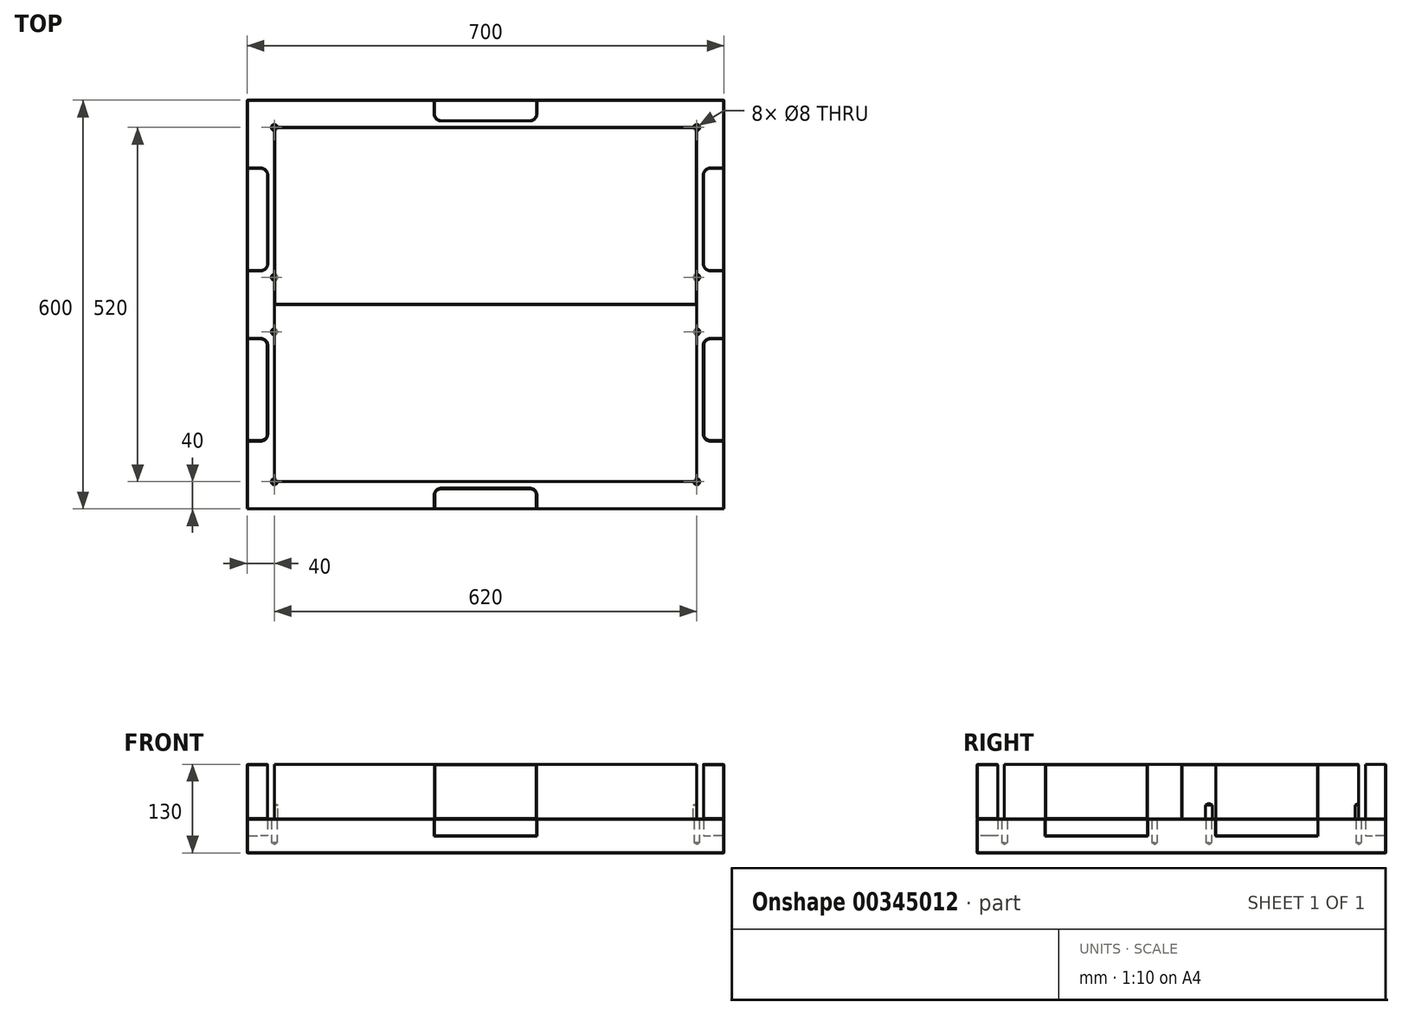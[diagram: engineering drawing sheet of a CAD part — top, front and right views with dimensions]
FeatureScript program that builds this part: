
annotation { "Feature Type Name" : "Feature", "Feature Type Description" : "" }
export const myFeature = defineFeature(function(context is Context, id is Id, definition is map)
    precondition{}
    {
        {
            var Q0;
            Q0=qCreatedBy(makeId("Top.planeOp"),FACE);
            var sketch = newSketch(context, id + "F0", { "sketchPlane" : qUnion([Q0])});
            skLineSegment(sketch, "E0", {"start": v(-350, 0) * mm, "end": v(350, 0) * mm, "construction": true});
            skLineSegment(sketch, "E1.bottom", {"start": v(350, -50) * mm, "end": v(330, -50) * mm});
            skLineSegment(sketch, "E1.top", {"start": v(350, -200) * mm, "end": v(330, -200) * mm});
            skLineSegment(sketch, "E1.left", {"start": v(350, -50) * mm, "end": v(350, -200) * mm});
            skLineSegment(sketch, "E1.right", {"start": v(320, -60) * mm, "end": v(320, -190) * mm});
            skPoint(sketch, "E2.visualSharp", {"position": v(320, -200) * mm});
            skArc(sketch, "E2.filletArc", {"start": v(320, -190) * mm, "mid": v(322.93, -197.07) * mm, "end": v(330, -200) * mm});
            skPoint(sketch, "E3.visualSharp", {"position": v(320, -50) * mm});
            skArc(sketch, "E3.filletArc", {"start": v(330, -50) * mm, "mid": v(322.93, -52.93) * mm, "end": v(320, -60) * mm});
            skLineSegment(sketch, "E4", {"start": v(0, 300) * mm, "end": v(0, -300) * mm, "construction": true});
            skLineSegment(sketch, "E5.MirrorCS", {"start": v(-350, -50) * mm, "end": v(-330, -50) * mm});
            skLineSegment(sketch, "E6.MirrorCS", {"start": v(-320, -60) * mm, "end": v(-320, -190) * mm});
            skArc(sketch, "E7.MirrorCS", {"start": v(-320, -190) * mm, "mid": v(-322.93, -197.07) * mm, "end": v(-330, -200) * mm});
            skArc(sketch, "E8.MirrorCS", {"start": v(-330, -50) * mm, "mid": v(-322.93, -52.93) * mm, "end": v(-320, -60) * mm});
            skLineSegment(sketch, "E9.MirrorCS", {"start": v(-350, -200) * mm, "end": v(-330, -200) * mm});
            skPoint(sketch, "E10", {"position": v(-310, 260) * mm});
            skPoint(sketch, "E11", {"position": v(310, 260) * mm});
            skPoint(sketch, "E12", {"position": v(310, -260) * mm});
            skPoint(sketch, "E13", {"position": v(-310, -260) * mm});
            skLineSegment(sketch, "E14.bottom", {"start": v(350, 300) * mm, "end": v(-350, 300) * mm});
            skLineSegment(sketch, "E14.top", {"start": v(350, -300) * mm, "end": v(-350, -300) * mm});
            skLineSegment(sketch, "E14.left", {"start": v(350, 300) * mm, "end": v(350, -300) * mm});
            skLineSegment(sketch, "E14.right", {"start": v(-350, 300) * mm, "end": v(-350, -300) * mm});
            skPoint(sketch, "E14.middle", {"position": v(0, 0) * mm});
            skLineSegment(sketch, "E15", {"start": v(-350, 125) * mm, "end": v(350, 125) * mm, "construction": true});
            skLineSegment(sketch, "E16", {"start": v(-350, -125) * mm, "end": v(350, -125) * mm, "construction": true});
            skLineSegment(sketch, "E17", {"start": v(320, -125) * mm, "end": v(350, -125) * mm, "construction": true});
            skLineSegment(sketch, "E18.bottom", {"start": v(330, 200) * mm, "end": v(350, 200) * mm});
            skLineSegment(sketch, "E18.top", {"start": v(330, 50) * mm, "end": v(350, 50) * mm});
            skLineSegment(sketch, "E18.left", {"start": v(320, 190) * mm, "end": v(320, 60) * mm});
            skLineSegment(sketch, "E18.right", {"start": v(350, 200) * mm, "end": v(350, 50) * mm});
            skLineSegment(sketch, "E19", {"start": v(320, 125) * mm, "end": v(350, 125) * mm, "construction": true});
            skPoint(sketch, "E20.visualSharp", {"position": v(320, 200) * mm});
            skArc(sketch, "E20.filletArc", {"start": v(330, 200) * mm, "mid": v(322.93, 197.07) * mm, "end": v(320, 190) * mm});
            skPoint(sketch, "E21.visualSharp", {"position": v(320, 50) * mm});
            skArc(sketch, "E21.filletArc", {"start": v(320, 60) * mm, "mid": v(322.93, 52.93) * mm, "end": v(330, 50) * mm});
            skLineSegment(sketch, "E22.bottom", {"start": v(-350, 200) * mm, "end": v(-330, 200) * mm});
            skLineSegment(sketch, "E22.top", {"start": v(-350, 50) * mm, "end": v(-330, 50) * mm});
            skLineSegment(sketch, "E22.left", {"start": v(-350, 200) * mm, "end": v(-350, 50) * mm});
            skLineSegment(sketch, "E22.right", {"start": v(-320, 190) * mm, "end": v(-320, 60) * mm});
            skLineSegment(sketch, "E23", {"start": v(-350, 125) * mm, "end": v(-320, 125) * mm, "construction": true});
            skPoint(sketch, "E24.visualSharp", {"position": v(-320, 200) * mm});
            skArc(sketch, "E24.filletArc", {"start": v(-320, 190) * mm, "mid": v(-322.93, 197.07) * mm, "end": v(-330, 200) * mm});
            skPoint(sketch, "E25.visualSharp", {"position": v(-320, 50) * mm});
            skArc(sketch, "E25.filletArc", {"start": v(-330, 50) * mm, "mid": v(-322.93, 52.93) * mm, "end": v(-320, 60) * mm});
            skLineSegment(sketch, "E26.bottom", {"start": v(-75, 300) * mm, "end": v(75, 300) * mm});
            skLineSegment(sketch, "E26.top", {"start": v(-65, 270) * mm, "end": v(65, 270) * mm});
            skLineSegment(sketch, "E26.left", {"start": v(-75, 300) * mm, "end": v(-75, 280) * mm});
            skLineSegment(sketch, "E26.right", {"start": v(75, 300) * mm, "end": v(75, 280) * mm});
            skLineSegment(sketch, "E27", {"start": v(0, 300) * mm, "end": v(0, 270) * mm, "construction": true});
            skPoint(sketch, "E28.visualSharp", {"position": v(-75, 270) * mm});
            skArc(sketch, "E28.filletArc", {"start": v(-75, 280) * mm, "mid": v(-72.07, 272.93) * mm, "end": v(-65, 270) * mm});
            skPoint(sketch, "E29.visualSharp", {"position": v(75, 270) * mm});
            skArc(sketch, "E29.filletArc", {"start": v(65, 270) * mm, "mid": v(72.07, 272.93) * mm, "end": v(75, 280) * mm});
            skLineSegment(sketch, "E30.bottom", {"start": v(-65, -270) * mm, "end": v(65, -270) * mm});
            skLineSegment(sketch, "E30.top", {"start": v(-75, -300) * mm, "end": v(75, -300) * mm});
            skLineSegment(sketch, "E30.left", {"start": v(-75, -280) * mm, "end": v(-75, -300) * mm});
            skLineSegment(sketch, "E30.right", {"start": v(75, -280) * mm, "end": v(75, -300) * mm});
            skLineSegment(sketch, "E31", {"start": v(0, -270) * mm, "end": v(0, -300) * mm, "construction": true});
            skPoint(sketch, "E32.visualSharp", {"position": v(-75, -270) * mm});
            skArc(sketch, "E32.filletArc", {"start": v(-65, -270) * mm, "mid": v(-72.07, -272.93) * mm, "end": v(-75, -280) * mm});
            skPoint(sketch, "E33.visualSharp", {"position": v(75, -270) * mm});
            skArc(sketch, "E33.filletArc", {"start": v(75, -280) * mm, "mid": v(72.07, -272.93) * mm, "end": v(65, -270) * mm});
            skSolve(sketch);
        }
        {
            var Q0;
            {var subQ14=sQuery(id+"F0.wireOp",EDGE,"E1.bottom");Q0=makeQuery(id+"F0.imprint","IMPRINT",FACE,{"disambiguationData":[TD([[makeQuery(id+"F0.imprint","IMPRINT",EDGE,{"derivedFrom":subQ14}),-1.0]])]});}
            extrude(context, id + "F1", {"entities" : qUnion([Q0]), "offsetDistance" : 25 * mm, "depth" : 50 * mm});
        }
        {
            var Q0;
            Q0=makeQuery(id+"F1.opExtrude","CAP_FACE",FACE,{"disambiguationData":[OSD([sQuery(id+"F0.wireOp",EDGE,"E1.bottom"),sQuery(id+"F0.wireOp",EDGE,"E1.top"),sQuery(id+"F0.wireOp",EDGE,"E1.right"),sQuery(id+"F0.wireOp",EDGE,"E2.filletArc"),sQuery(id+"F0.wireOp",EDGE,"E3.filletArc"),sQuery(id+"F0.wireOp",EDGE,"E5.MirrorCS"),sQuery(id+"F0.wireOp",EDGE,"E6.MirrorCS"),sQuery(id+"F0.wireOp",EDGE,"E7.MirrorCS"),sQuery(id+"F0.wireOp",EDGE,"E8.MirrorCS"),sQuery(id+"F0.wireOp",EDGE,"E9.MirrorCS"),sQuery(id+"F0.wireOp",EDGE,"E14.bottom"),sQuery(id+"F0.wireOp",EDGE,"E14.top"),sQuery(id+"F0.wireOp",EDGE,"E14.left"),sQuery(id+"F0.wireOp",EDGE,"E14.right")])],"isStart":false});
            var sketch = newSketch(context, id + "F2", { "sketchPlane" : qUnion([Q0])});
            skLineSegment(sketch, "E34.bottom", {"start": v(-350, 300) * mm, "end": v(350, 300) * mm});
            skLineSegment(sketch, "E34.top", {"start": v(-350, -300) * mm, "end": v(350, -300) * mm});
            skLineSegment(sketch, "E34.left", {"start": v(-350, 300) * mm, "end": v(-350, -300) * mm});
            skLineSegment(sketch, "E34.right", {"start": v(350, 300) * mm, "end": v(350, -300) * mm});
            skLineSegment(sketch, "E35.0", {"start": v(-310, 260) * mm, "end": v(310, 260) * mm});
            skLineSegment(sketch, "E35.1", {"start": v(-310, 260) * mm, "end": v(-310, -260) * mm});
            skLineSegment(sketch, "E35.2", {"start": v(-310, -260) * mm, "end": v(310, -260) * mm});
            skLineSegment(sketch, "E35.3", {"start": v(310, 260) * mm, "end": v(310, -260) * mm});
            skLineSegment(sketch, "E36", {"start": v(350, 0) * mm, "end": v(-350, 0) * mm});
            skLineSegment(sketch, "E37", {"start": v(310, 40) * mm, "end": v(-310, 40) * mm});
            skLineSegment(sketch, "E38", {"start": v(310, -40) * mm, "end": v(-310, -40) * mm});
            skSolve(sketch);
        }
        {
            var Q0;
            {var subQ9=sQuery(id+"F2.wireOp",EDGE,"E35.2");Q0=makeQuery(id+"F2.imprint","IMPRINT",FACE,{"disambiguationData":[TD([[makeQuery(id+"F2.imprint","IMPRINT",EDGE,{"derivedFrom":subQ9}),-1.0]])]});}
            var Q1;
            {var subQ1=makeQuery(id+"F1.opExtrude","CAP_EDGE",EDGE,{"disambiguationData":[OSD([sQuery(id+"F0.wireOp",EDGE,"E1.bottom")])],"isStart":false});Q1=makeQuery(id+"F2.imprint","IMPRINT",FACE,{"disambiguationData":[TD([[makeQuery(id+"F2.imprint","IMPRINT",EDGE,{"derivedFrom":subQ1}),1.0]])]});}
            var Q2;
            Q2=makeQuery(id+"F2.imprint","IMPRINT",FACE,{"disambiguationData":[TD([[makeQuery(id+"F2.imprint","IMPRINT",EDGE,{"derivedFrom":makeQuery(id+"F1.opExtrude","CAP_EDGE",EDGE,{"disambiguationData":[OSD([sQuery(id+"F0.wireOp",EDGE,"E30.bottom")])],"isStart":false})}),-1.0]])]});
            var Q3;
            {var subQ0=makeQuery(id+"F1.opExtrude","CAP_EDGE",EDGE,{"disambiguationData":[OSD([sQuery(id+"F0.wireOp",EDGE,"E5.MirrorCS")])],"isStart":false});Q3=makeQuery(id+"F2.imprint","IMPRINT",FACE,{"disambiguationData":[TD([[makeQuery(id+"F2.imprint","IMPRINT",EDGE,{"derivedFrom":subQ0}),-1.0]])]});}
            var Q4;
            {var subQ0=sQuery(id+"F2.wireOp",EDGE,"E35.2");Q4=makeQuery(id+"F2.imprint","IMPRINT",FACE,{"disambiguationData":[TD([[makeQuery(id+"F2.imprint","IMPRINT",EDGE,{"derivedFrom":subQ0}),1.0]])]});}
            var Q5;
            {var subQ0=sQuery(id+"F2.wireOp",EDGE,"E38");Q5=makeQuery(id+"F2.imprint","IMPRINT",FACE,{"disambiguationData":[TD([[makeQuery(id+"F2.imprint","IMPRINT",EDGE,{"derivedFrom":subQ0}),-1.0]])]});}
            extrude(context, id + "F3", {"entities" : qUnion([Q0, Q1, Q2, Q3, Q4, Q5]), "flatOperationType" : FlatOperationType.REMOVE, "offsetDistance" : 25 * mm, "depth" : 80 * mm, "domain" : OperationDomain.MODEL});
        }
        {
            var Q0;
            {var subQ8=sQuery(id+"F2.wireOp",EDGE,"E35.0");Q0=makeQuery(id+"F2.imprint","IMPRINT",FACE,{"disambiguationData":[TD([[makeQuery(id+"F2.imprint","IMPRINT",EDGE,{"derivedFrom":subQ8}),1.0]])]});}
            var Q1;
            {var subQ0=makeQuery(id+"F1.opExtrude","CAP_EDGE",EDGE,{"disambiguationData":[OSD([sQuery(id+"F0.wireOp",EDGE,"E18.bottom")])],"isStart":false});Q1=makeQuery(id+"F2.imprint","IMPRINT",FACE,{"disambiguationData":[TD([[makeQuery(id+"F2.imprint","IMPRINT",EDGE,{"derivedFrom":subQ0}),-1.0]])]});}
            var Q2;
            Q2=makeQuery(id+"F2.imprint","IMPRINT",FACE,{"disambiguationData":[TD([[makeQuery(id+"F2.imprint","IMPRINT",EDGE,{"derivedFrom":makeQuery(id+"F1.opExtrude","CAP_EDGE",EDGE,{"disambiguationData":[OSD([sQuery(id+"F0.wireOp",EDGE,"E26.top")])],"isStart":false})}),1.0]])]});
            var Q3;
            {var subQ1=makeQuery(id+"F1.opExtrude","CAP_EDGE",EDGE,{"disambiguationData":[OSD([sQuery(id+"F0.wireOp",EDGE,"E22.bottom")])],"isStart":false});Q3=makeQuery(id+"F2.imprint","IMPRINT",FACE,{"disambiguationData":[TD([[makeQuery(id+"F2.imprint","IMPRINT",EDGE,{"derivedFrom":subQ1}),-1.0]])]});}
            var Q4;
            {var subQ0=sQuery(id+"F2.wireOp",EDGE,"E35.0");Q4=makeQuery(id+"F2.imprint","IMPRINT",FACE,{"disambiguationData":[TD([[makeQuery(id+"F2.imprint","IMPRINT",EDGE,{"derivedFrom":subQ0}),-1.0]])]});}
            var Q5;
            {var subQ0=sQuery(id+"F2.wireOp",EDGE,"E37");Q5=makeQuery(id+"F2.imprint","IMPRINT",FACE,{"disambiguationData":[TD([[makeQuery(id+"F2.imprint","IMPRINT",EDGE,{"derivedFrom":subQ0}),1.0]])]});}
            extrude(context, id + "F4", {"entities" : qUnion([Q0, Q1, Q2, Q3, Q4, Q5]), "flatOperationType" : FlatOperationType.REMOVE, "depth" : 80 * mm, "offsetDistance" : 25 * mm, "domain" : OperationDomain.MODEL});
        }
        {
            var Q0;
            Q0=makeQuery(id+"F3.opExtrude","CAP_FACE",FACE,{"disambiguationData":[OSD([sQuery(id+"F2.wireOp",EDGE,"E34.bottom"),sQuery(id+"F2.wireOp",EDGE,"E34.top"),sQuery(id+"F2.wireOp",EDGE,"E34.left"),sQuery(id+"F2.wireOp",EDGE,"E34.right")])],"isStart":false});
            var Q1;
            Q1=makeQuery(id+"F3.opExtrude","CAP_FACE",FACE,{"disambiguationData":[OSD([sQuery(id+"F2.wireOp",EDGE,"E34.bottom"),sQuery(id+"F2.wireOp",EDGE,"E34.top"),sQuery(id+"F2.wireOp",EDGE,"E34.left"),sQuery(id+"F2.wireOp",EDGE,"E34.right")])],"isStart":true});
            var Q2;
            Q2=makeQuery(id+"F3.opExtrude","SWEPT_EDGE",EDGE,{"disambiguationData":[OSD([sQuery(id+"F2.wireOp",EDGE,"E34.bottom"),sQuery(id+"F2.wireOp",EDGE,"E34.right")])]});
            var Q3;
            Q3=makeQuery(id+"F3.opExtrude","SWEPT_EDGE",EDGE,{"disambiguationData":[OSD([sQuery(id+"F2.wireOp",EDGE,"E34.bottom"),sQuery(id+"F2.wireOp",EDGE,"E34.left")])]});
            var Q4;
            Q4=makeQuery(id+"F3.opExtrude","SWEPT_EDGE",EDGE,{"disambiguationData":[OSD([sQuery(id+"F2.wireOp",EDGE,"E34.top"),sQuery(id+"F2.wireOp",EDGE,"E34.left")])]});
            var Q5;
            Q5=makeQuery(id+"F3.opExtrude","SWEPT_EDGE",EDGE,{"disambiguationData":[OSD([sQuery(id+"F2.wireOp",EDGE,"E34.top"),sQuery(id+"F2.wireOp",EDGE,"E34.right")])]});
            var Q6;
            Q6=makeQuery(id+"F4.opExtrude","CAP_EDGE",EDGE,{"disambiguationData":[OSD([sQuery(id+"F2.wireOp",EDGE,"E34.right")])],"isStart":false});
            var Q7;
            Q7=makeQuery(id+"F4.opExtrude","CAP_EDGE",EDGE,{"disambiguationData":[OSD([sQuery(id+"F2.wireOp",EDGE,"E34.bottom")])],"isStart":false});
            var Q8;
            Q8=makeQuery(id+"F4.opExtrude","CAP_EDGE",EDGE,{"disambiguationData":[OSD([sQuery(id+"F2.wireOp",EDGE,"E36")])],"isStart":false});
            var Q9;
            Q9=makeQuery(id+"F4.opExtrude","CAP_EDGE",EDGE,{"disambiguationData":[OSD([sQuery(id+"F2.wireOp",EDGE,"E34.left")])],"isStart":false});
            var Q10;
            Q10=makeQuery(id+"F4.opExtrude","SWEPT_EDGE",EDGE,{"disambiguationData":[OSD([sQuery(id+"F2.wireOp",EDGE,"E34.left"),sQuery(id+"F2.wireOp",EDGE,"E36")])]});
            var Q11;
            Q11=makeQuery(id+"F4.opExtrude","CAP_FACE",FACE,{"disambiguationData":[OSD([sQuery(id+"F2.wireOp",EDGE,"E34.bottom"),sQuery(id+"F2.wireOp",EDGE,"E34.left"),sQuery(id+"F2.wireOp",EDGE,"E34.right"),sQuery(id+"F2.wireOp",EDGE,"E36")])],"isStart":false});
            var Q12;
            Q12=makeQuery(id+"F4.opExtrude","SWEPT_EDGE",EDGE,{"disambiguationData":[OSD([sQuery(id+"F2.wireOp",EDGE,"E34.bottom"),sQuery(id+"F2.wireOp",EDGE,"E34.right")])]});
            var Q13;
            Q13=makeQuery(id+"F4.opExtrude","SWEPT_EDGE",EDGE,{"disambiguationData":[OSD([sQuery(id+"F2.wireOp",EDGE,"E34.bottom"),sQuery(id+"F2.wireOp",EDGE,"E34.left")])]});
            chamfer(context, id + "F5", {"entities" : qUnion([Q0, Q1, Q2, Q3, Q4, Q5, Q6, Q7, Q8, Q9, Q10, Q11, Q12, Q13]), "width" : 0.5 * mm, "tangentPropagation" : true});
        }
        {
            var Q0;
            Q0=sQuery(id+"F2.wireOp",VERTEX,"E35.1.start");
            var Q1;
            Q1=sQuery(id+"F2.wireOp",VERTEX,"E35.0.end");
            var Q2;
            Q2=sQuery(id+"F2.wireOp",VERTEX,"E35.3.end");
            var Q3;
            Q3=sQuery(id+"F2.wireOp",VERTEX,"E35.2.start");
            var Q4;
            Q4=sQuery(id+"F2.wireOp",VERTEX,"E37.start");
            var Q5;
            Q5=sQuery(id+"F2.wireOp",VERTEX,"E38.end");
            var Q6;
            Q6=sQuery(id+"F2.wireOp",VERTEX,"E38.start");
            var Q7;
            Q7=sQuery(id+"F2.wireOp",VERTEX,"E37.end");
            var Q8;
            Q8=makeQuery(id+"F3.opExtrude","SWEPT_BODY",BODY,{"disambiguationData":[OSD([sQuery(id+"F2.wireOp",EDGE,"E34.bottom"),sQuery(id+"F2.wireOp",EDGE,"E34.top"),sQuery(id+"F2.wireOp",EDGE,"E34.left"),sQuery(id+"F2.wireOp",EDGE,"E34.right")])]});
            var Q9;
            Q9=makeQuery(id+"F4.opExtrude","SWEPT_BODY",BODY,{"disambiguationData":[OSD([sQuery(id+"F2.wireOp",EDGE,"E34.bottom"),sQuery(id+"F2.wireOp",EDGE,"E34.left"),sQuery(id+"F2.wireOp",EDGE,"E34.right"),sQuery(id+"F2.wireOp",EDGE,"E36")])]});
            hole(context, id + "F6", {"style" : HoleStyle.SIMPLE, "endStyle" : HoleEndStyle.BLIND, "oppositeDirection" : true, "holeDiameter" : 10 * mm, "majorDiameter" : 5 * mm, "holeDepth" : 20 * mm, "isTappedThrough" : true, "tappedDepth" : 12 * mm, "tapClearance" : 3, "locations" : qUnion([Q0, Q1, Q2, Q3, Q4, Q5, Q6, Q7]), "scope" : qUnion([Q8, Q9]), "startStyle" : HoleStartStyle.PART});
        }
        {
            var Q0;
            Q0 = qSketchRegion(id + "F0", true);
            var Q1;
            Q1 = qConstructionFilter(qBodyType(qCreatedBy(id + "F0" ,EDGE), BodyType.WIRE), ConstructionObject.NO);
            extrude(context, id + "F7", {"entities" : qUnion([Q0]), "operationType" : NewBodyOperationType.ADD, "surfaceEntities" : qUnion([Q1]), "offsetDistance" : 25 * mm, "depth" : 25 * mm});
        }
        {
            var Q0;
            Q0=sQuery(id+"F2.wireOp",VERTEX,"E35.1.start");
            var Q1;
            Q1=sQuery(id+"F2.wireOp",VERTEX,"E35.0.end");
            var Q2;
            Q2=sQuery(id+"F2.wireOp",VERTEX,"E35.3.end");
            var Q3;
            Q3=sQuery(id+"F2.wireOp",VERTEX,"E35.2.start");
            var Q4;
            Q4=sQuery(id+"F2.wireOp",VERTEX,"E37.start");
            var Q5;
            Q5=sQuery(id+"F2.wireOp",VERTEX,"E37.end");
            var Q6;
            Q6=sQuery(id+"F2.wireOp",VERTEX,"E38.end");
            var Q7;
            Q7=sQuery(id+"F2.wireOp",VERTEX,"E38.start");
            var Q8;
            Q8=makeQuery(id+"F1.opExtrude","SWEPT_BODY",BODY,{"disambiguationData":[OSD([sQuery(id+"F0.wireOp",EDGE,"9696f999-dd8b-4db2-95aa-c8651f8d9f2f.bottom"),sQuery(id+"F0.wireOp",EDGE,"9696f999-dd8b-4db2-95aa-c8651f8d9f2f.top"),sQuery(id+"F0.wireOp",EDGE,"9696f999-dd8b-4db2-95aa-c8651f8d9f2f.left"),sQuery(id+"F0.wireOp",EDGE,"9696f999-dd8b-4db2-95aa-c8651f8d9f2f.right"),sQuery(id+"F0.wireOp",EDGE,"E1.bottom"),sQuery(id+"F0.wireOp",EDGE,"E1.top"),sQuery(id+"F0.wireOp",EDGE,"E1.right"),sQuery(id+"F0.wireOp",EDGE,"E2.filletArc"),sQuery(id+"F0.wireOp",EDGE,"E3.filletArc"),sQuery(id+"F0.wireOp",EDGE,"E5.MirrorCS"),sQuery(id+"F0.wireOp",EDGE,"E6.MirrorCS"),sQuery(id+"F0.wireOp",EDGE,"E7.MirrorCS"),sQuery(id+"F0.wireOp",EDGE,"E8.MirrorCS"),sQuery(id+"F0.wireOp",EDGE,"E9.MirrorCS")])]});
            hole(context, id + "F8", {"style" : HoleStyle.SIMPLE, "endStyle" : HoleEndStyle.BLIND, "holeDiameter" : 8 * mm, "majorDiameter" : 5 * mm, "holeDepth" : 35 * mm, "isTappedThrough" : true, "tappedDepth" : 12 * mm, "tapClearance" : 3, "locations" : qUnion([Q0, Q1, Q2, Q3, Q4, Q5, Q6, Q7]), "scope" : qUnion([Q8]), "startStyle" : HoleStartStyle.SKETCH});
        }
        {
            var Q0;
            Q0=makeQuery(id+"F1.opExtrude","CAP_FACE",FACE,{"disambiguationData":[OSD([sQuery(id+"F0.wireOp",EDGE,"E1.bottom"),sQuery(id+"F0.wireOp",EDGE,"E1.top"),sQuery(id+"F0.wireOp",EDGE,"E1.right"),sQuery(id+"F0.wireOp",EDGE,"E2.filletArc"),sQuery(id+"F0.wireOp",EDGE,"E3.filletArc"),sQuery(id+"F0.wireOp",EDGE,"E5.MirrorCS"),sQuery(id+"F0.wireOp",EDGE,"E6.MirrorCS"),sQuery(id+"F0.wireOp",EDGE,"E7.MirrorCS"),sQuery(id+"F0.wireOp",EDGE,"E8.MirrorCS"),sQuery(id+"F0.wireOp",EDGE,"E9.MirrorCS"),sQuery(id+"F0.wireOp",EDGE,"E14.bottom"),sQuery(id+"F0.wireOp",EDGE,"E14.top"),sQuery(id+"F0.wireOp",EDGE,"E14.left"),sQuery(id+"F0.wireOp",EDGE,"E14.right")])],"isStart":false});
            var Q1;
            {var subQ0=sQuery(id+"F0.wireOp",EDGE,"E14.right");var subQ1=sQuery(id+"F0.wireOp",EDGE,"E14.left");var subQ2=sQuery(id+"F0.wireOp",EDGE,"E14.top");var subQ3=sQuery(id+"F0.wireOp",EDGE,"E14.bottom");Q1=makeQuery(id+"F7.boolean.opBoolean","MERGE",FACE,{"derivedFrom":[makeQuery(id+"F1.opExtrude","CAP_FACE",FACE,{"disambiguationData":[OSD([sQuery(id+"F0.wireOp",EDGE,"E1.bottom"),sQuery(id+"F0.wireOp",EDGE,"E1.top"),sQuery(id+"F0.wireOp",EDGE,"E1.right"),sQuery(id+"F0.wireOp",EDGE,"E2.filletArc"),sQuery(id+"F0.wireOp",EDGE,"E3.filletArc"),sQuery(id+"F0.wireOp",EDGE,"E5.MirrorCS"),sQuery(id+"F0.wireOp",EDGE,"E6.MirrorCS"),sQuery(id+"F0.wireOp",EDGE,"E7.MirrorCS"),sQuery(id+"F0.wireOp",EDGE,"E8.MirrorCS"),sQuery(id+"F0.wireOp",EDGE,"E9.MirrorCS"),subQ3,subQ2,subQ1,subQ0])],"isStart":true}),makeQuery(id+"F7.opExtrude","CAP_FACE",FACE,{"disambiguationData":[OSD([subQ3,subQ2,subQ1,subQ0])],"isStart":true})]});}
            var Q2;
            Q2=makeQuery(id+"F1.opExtrude","SWEPT_FACE",FACE,{"disambiguationData":[OSD([sQuery(id+"F0.wireOp",EDGE,"E14.top")])]});
            var Q3;
            {var subQ0=sQuery(id+"F0.wireOp",EDGE,"E14.left");Q3=makeQuery(id+"F7.boolean.opBoolean","MERGE",FACE,{"derivedFrom":[makeQuery(id+"F1.opExtrude","SWEPT_FACE",FACE,{"disambiguationData":[OSD([subQ0]),TDD([makeQuery(id+"F0.imprint","IMPRINT",EDGE,{"disambiguationData":[TD([[makeQuery(id+"F0.imprint","INTERSECT",VERTEX,{"derivedFrom":[sQuery(id+"F0.wireOp",EDGE,"E1.bottom"),subQ0]}),1.0]])],"derivedFrom":subQ0})])]}),makeQuery(id+"F1.opExtrude","SWEPT_FACE",FACE,{"disambiguationData":[OSD([subQ0]),TDD([makeQuery(id+"F0.imprint","IMPRINT",EDGE,{"disambiguationData":[TD([[makeQuery(id+"F0.imprint","INTERSECT",VERTEX,{"derivedFrom":[sQuery(id+"F0.wireOp",EDGE,"E1.top"),subQ0]}),-1.0]])],"derivedFrom":subQ0})])]}),makeQuery(id+"F7.opExtrude","SWEPT_FACE",FACE,{"disambiguationData":[OSD([subQ0])]})]});}
            var Q4;
            {var subQ0=sQuery(id+"F0.wireOp",EDGE,"E14.right");Q4=makeQuery(id+"F7.boolean.opBoolean","MERGE",FACE,{"derivedFrom":[makeQuery(id+"F1.opExtrude","SWEPT_FACE",FACE,{"disambiguationData":[OSD([subQ0]),TDD([makeQuery(id+"F0.imprint","IMPRINT",EDGE,{"disambiguationData":[TD([[makeQuery(id+"F0.imprint","INTERSECT",VERTEX,{"derivedFrom":[sQuery(id+"F0.wireOp",EDGE,"E5.MirrorCS"),subQ0]}),1.0]])],"derivedFrom":subQ0})])]}),makeQuery(id+"F1.opExtrude","SWEPT_FACE",FACE,{"disambiguationData":[OSD([subQ0]),TDD([makeQuery(id+"F0.imprint","IMPRINT",EDGE,{"disambiguationData":[TD([[makeQuery(id+"F0.imprint","INTERSECT",VERTEX,{"derivedFrom":[sQuery(id+"F0.wireOp",EDGE,"E9.MirrorCS"),subQ0]}),-1.0]])],"derivedFrom":subQ0})])]}),makeQuery(id+"F7.opExtrude","SWEPT_FACE",FACE,{"disambiguationData":[OSD([subQ0])]})]});}
            var Q5;
            Q5=makeQuery(id+"F1.opExtrude","SWEPT_FACE",FACE,{"disambiguationData":[OSD([sQuery(id+"F0.wireOp",EDGE,"E14.bottom")])]});
            chamfer(context, id + "F9", {"entities" : qUnion([Q0, Q1, Q2, Q3, Q4, Q5]), "width" : 0.5 * mm, "tangentPropagation" : true});
        }
    });
